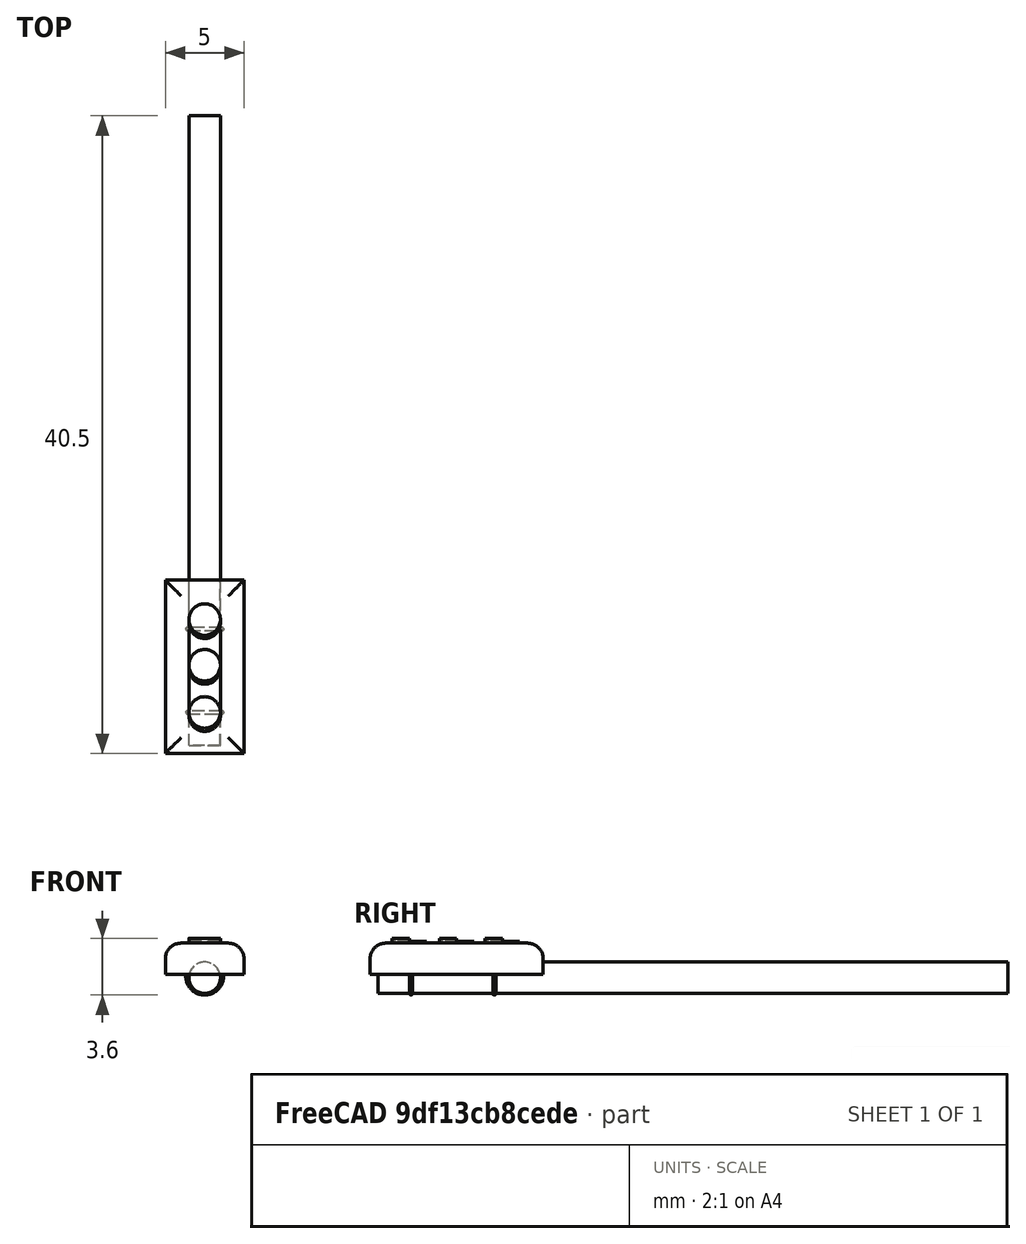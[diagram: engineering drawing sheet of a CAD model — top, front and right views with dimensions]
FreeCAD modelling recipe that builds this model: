
FCSTD DOCUMENT  (FreeCAD 0.18R4 (GitTag))
Label: Semaforo Reto
License: All rights reserved
LicenseURL: http://en.wikipedia.org/wiki/All_rights_reserved
objects: Part::Cylinder×10, Part::MultiFuse×5, Part::Cut×3, Part::Torus×2, Part::Box×1, Part::Fillet×1, Part::Fuse×1
note: 23 computed .brp shape members not serialized (recipe doc carries the construction recipe); baked Part::Feature solids carry a one-line shape summary decoded from their .brp

FEATURE [Part::Cylinder] Cylinder  label="Cilindro"
  Angle = 360
  AttacherType = Attacher::AttachEngine3D
  Height = 1
  Placement = pos=(2.5,5.6,1.1) rot=(0,0,1;0rad)
  Radius = 1
FEATURE [Part::Box] Box  label="Cubo"
  AttacherType = Attacher::AttachEngine3D
  Height = 2
  Length = 5
  Width = 11
FEATURE [Part::Cylinder] Cylinder001  label="Cilindro001"
  Angle = 360
  AttacherType = Attacher::AttachEngine3D
  Height = 1
  Placement = pos=(2.5,2.6,1.1) rot=(0,0,1;0rad)
  Radius = 1
FEATURE [Part::Cylinder] Cylinder002  label="Cilindro002"
  Angle = 360
  AttacherType = Attacher::AttachEngine3D
  Height = 1
  Placement = pos=(2.5,8.5,1.1) rot=(0,0,1;0rad)
  Radius = 1
FEATURE [Part::Fillet] Fillet
  Base = -> Box
  Edges = 4 edges r=1: [Edge2,Edge6,Edge10,Edge12]
FEATURE [Part::MultiFuse] Fusion
  Refine = true
  Shapes = -> [Fillet,Cylinder002,Cylinder001,Cylinder]
FEATURE [Part::Cylinder] Cylinder003  label="Cilindro003"
  Angle = 360
  AttacherType = Attacher::AttachEngine3D
  Height = 40
  Placement = pos=(2.5,0.5,-0.2) rot=(-0.57735,0.57735,0.57735;2.0944rad)
  Radius = 1
FEATURE [Part::Torus] Torus  label="Toro"
  Angle1 = -180
  Angle2 = 180
  Angle3 = 360
  AttacherType = Attacher::AttachEngine3D
  Placement = pos=(2.5,2.6,-0.1) rot=(1,0,0;4.71239rad)
  Radius1 = 1.1
  Radius2 = 0.1
FEATURE [Part::Torus] Torus001  label="Toro001"
  Angle1 = -180
  Angle2 = 180
  Angle3 = 360
  AttacherType = Attacher::AttachEngine3D
  Placement = pos=(2.5,7.9,-0.1) rot=(-1,0,0;1.5708rad)
  Radius1 = 1.1
  Radius2 = 0.1
FEATURE [Part::Fuse] Fusion001
  Base = -> Cylinder003
  Refine = true
  Tool = -> Torus
FEATURE [Part::MultiFuse] Fusion002
  Refine = true
  Shapes = -> [Fusion001,Torus001]
FEATURE [Part::MultiFuse] Fusion003
  Refine = true
  Shapes = -> [Fusion002,Fusion]
FEATURE [Part::Cylinder] Cylinder004  label="Cilindro004"
  Angle = 360
  AttacherType = Attacher::AttachEngine3D
  Height = 1
  Radius = 1
FEATURE [Part::Cylinder] Cylinder005  label="Cilindro005"
  Angle = 360
  AttacherType = Attacher::AttachEngine3D
  Height = 1
  Placement = pos=(0,0.2,0) rot=(0,0,1;0rad)
  Radius = 1
FEATURE [Part::Cut] Cut
  Base = -> Cylinder004
  Placement = pos=(2.5,2.4,1.3) rot=(0,0,1;0rad)
  Refine = true
  Tool = -> Cylinder005
FEATURE [Part::Cylinder] Cylinder006  label="Cilindro006"
  Angle = 360
  AttacherType = Attacher::AttachEngine3D
  Height = 1
  Placement = pos=(0,0.2,0) rot=(0,0,1;0rad)
  Radius = 1
FEATURE [Part::Cylinder] Cylinder007  label="Cilindro007"
  Angle = 360
  AttacherType = Attacher::AttachEngine3D
  Height = 1
  Radius = 1
FEATURE [Part::Cut] Cut001
  Base = -> Cylinder007
  Placement = pos=(2.5,5.4,1.3) rot=(0,0,1;0rad)
  Refine = true
  Tool = -> Cylinder006
FEATURE [Part::Cylinder] Cylinder008  label="Cilindro008"
  Angle = 360
  AttacherType = Attacher::AttachEngine3D
  Height = 1
  Placement = pos=(0,0.2,0) rot=(0,0,1;0rad)
  Radius = 1
FEATURE [Part::Cylinder] Cylinder009  label="Cilindro009"
  Angle = 360
  AttacherType = Attacher::AttachEngine3D
  Height = 1
  Radius = 1
FEATURE [Part::Cut] Cut002
  Base = -> Cylinder009
  Placement = pos=(2.5,8.3,1.3) rot=(0,0,1;0rad)
  Refine = true
  Tool = -> Cylinder008
FEATURE [Part::MultiFuse] Fusion004
  Refine = true
  Shapes = -> [Cut,Cut001,Cut002]
FEATURE [Part::MultiFuse] Fusion005
  Refine = true
  Shapes = -> [Fusion003,Fusion004]
